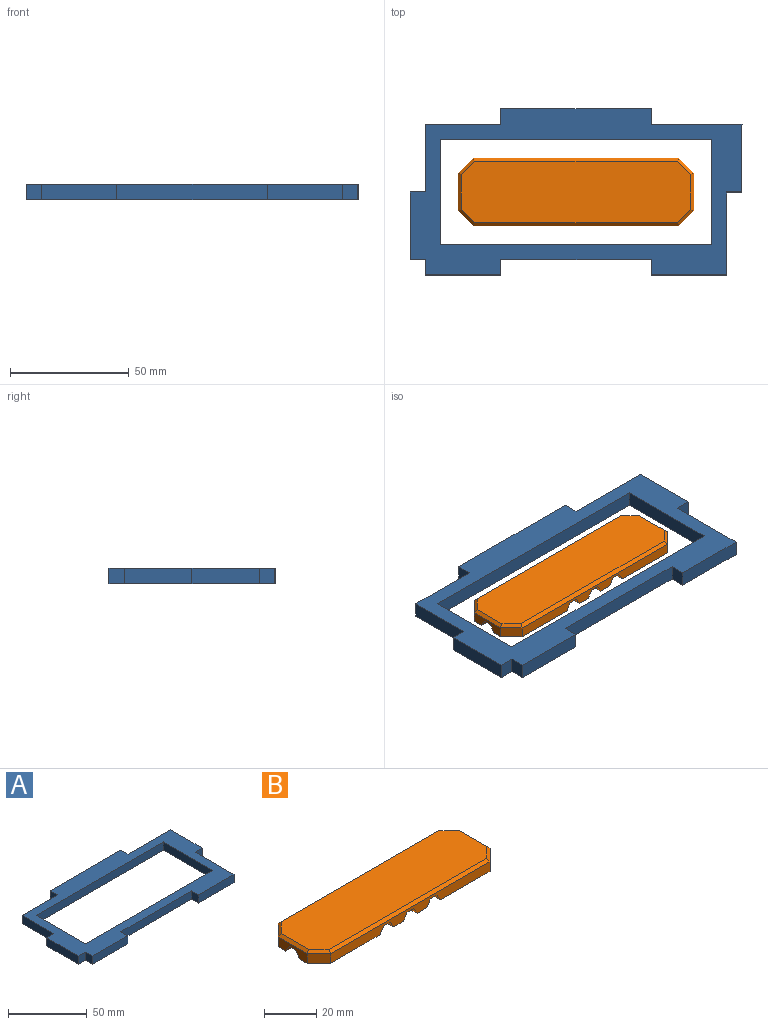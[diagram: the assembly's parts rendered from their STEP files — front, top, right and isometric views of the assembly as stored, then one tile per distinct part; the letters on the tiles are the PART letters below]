
ASSEMBLY  parts=2 mates=1
PART A: 24 faces, bbox 139.7x69.9x6.4 mm
  f0: plane 44.45x6.35mm, normal (-1,0,0), area 282.3mm2, adj f1,f21,f22,f23
  f1: plane 114.3x6.35mm, normal (0,1,0), area 725.8mm2, adj f0,f2,f22,f23
  f2: plane 44.45x6.35mm, normal (1,0,0), area 282.3mm2, adj f1,f21,f22,f23
  f3: plane 6.35x6.35mm, normal (1,0,0), area 40.3mm2, adj f4,f20,f22,f23
  f4: plane 63.5x6.35mm, normal (0,-1,0), area 403.2mm2, adj f3,f5,f22,f23
  f5: plane 6.35x6.35mm, normal (-1,0,0), area 40.3mm2, adj f4,f6,f22,f23
  f6: plane 31.75x6.35mm, normal (0,-1,0), area 201.6mm2, adj f5,f7,f22,f23
  f7: plane 34.93x6.35mm, normal (1,0,0), area 221.8mm2, adj f6,f8,f22,f23
  f8: plane 6.35x6.35mm, normal (0,-1,0), area 40.3mm2, adj f7,f9,f22,f23
  f9: plane 28.58x6.35mm, normal (1,0,0), area 181.5mm2, adj f8,f10,f22,f23
  f10: plane 38.1x6.35mm, normal (0,1,0), area 241.9mm2, adj f9,f11,f22,f23
  f11: plane 6.35x6.35mm, normal (1,0,0), area 40.3mm2, adj f10,f12,f22,f23
  f12: plane 63.5x6.35mm, normal (0,1,0), area 403.2mm2, adj f11,f13,f22,f23
  f13: plane 6.35x6.35mm, normal (-1,0,0), area 40.3mm2, adj f12,f14,f22,f23
  f14: plane 31.75x6.35mm, normal (0,1,0), area 201.6mm2, adj f13,f15,f22,f23
  f15: plane 28.58x6.35mm, normal (-1,0,0), area 181.5mm2, adj f14,f16,f22,f23
  f16: plane 6.35x6.35mm, normal (0,1,0), area 40.3mm2, adj f15,f17,f22,f23
  f17: plane 28.58x6.35mm, normal (-1,0,0), area 181.5mm2, adj f16,f18,f22,f23
  f18: plane 6.35x6.35mm, normal (0,-1,0), area 40.3mm2, adj f17,f19,f22,f23
  f19: plane 6.35x6.35mm, normal (-1,0,0), area 40.3mm2, adj f18,f20,f22,f23
  f20: plane 31.75x6.35mm, normal (0,-1,0), area 201.6mm2, adj f3,f19,f22,f23
  f21: plane 114.3x6.35mm, normal (0,-1,0), area 725.8mm2, adj f0,f2,f22,f23
  f22: plane 139.7x69.85mm, normal (0,0,1), area 3346.8mm2, adj f0,f1,f2,f3,f4,f5,f6,f7
  f23: plane 139.7x69.85mm, normal (0,0,-1), area 3346.8mm2, adj f0,f1,f2,f3,f4,f5,f6,f7
PART B: 42 faces, bbox 99.1x28.4x5.7 mm
  f0: plane 33.16x28.45mm, normal (0,0,-1), area 746.7mm2, adj f4,f5,f16,f17,f18,f20,f23,f24
  f1: plane 28.45x5.37mm, normal (0,0,-1), area 152.7mm2, adj f4,f5,f37,f40
  f2: plane 28.45x5.37mm, normal (0,0,-1), area 152.7mm2, adj f4,f5,f34,f36
  f3: plane 33.16x28.45mm, normal (0,0,-1), area 839.8mm2, adj f4,f5,f19,f21,f22,f27,f31,f33
  f4: plane 86.36x4.45mm, normal (0,1,0), area 331.5mm2, adj f0,f1,f2,f3,f10,f19,f20,f33
  f5: plane 86.36x4.45mm, normal (0,-1,0), area 331.5mm2, adj f0,f1,f2,f3,f8,f21,f23,f33
  f6: plane 96.52x25.91mm, normal (0,0,1), area 2437.8mm2, adj f7,f8,f9,f10,f11,f12,f13,f14
  f7: plane 15.75x1.27mm, normal (-0.71,0,0.71), area 27.3mm2, adj f6,f11,f12,f24
  f8: plane 86.36x1.27mm, normal (0,-0.71,0.71), area 154.2mm2, adj f5,f6,f12,f14
  f9: plane 15.75x1.27mm, normal (0.71,0,0.71), area 27.3mm2, adj f6,f13,f14,f22
  f10: plane 86.36x1.27mm, normal (0,0.71,0.71), area 154.2mm2, adj f4,f6,f11,f13
  f11: plane 6.88x6.88mm, normal (-0.5,0.5,0.71), area 15.2mm2, adj f6,f7,f10,f20
  f12: plane 6.88x6.88mm, normal (-0.5,-0.5,0.71), area 15.2mm2, adj f6,f7,f8,f23
  f13: plane 6.88x6.88mm, normal (0.5,0.5,0.71), area 15.2mm2, adj f6,f9,f10,f19
  f14: plane 6.88x6.88mm, normal (0.5,-0.5,0.71), area 15.2mm2, adj f6,f8,f9,f21
  f15: plane 12.7x3.67mm, normal (0,0,-1), area 46.6mm2, adj f16,f17,f18,f24
  f16: plane 7.33x3.18mm, normal (-1,0,0), area 17.5mm2, adj f0,f15,f17,f18
  f17: plane 12.7x3.18mm, normal (0,-0.87,-0.5), area 46.6mm2, adj f0,f15,f16,f24
  f18: plane 12.7x3.18mm, normal (0,0.87,-0.5), area 46.6mm2, adj f0,f15,f16,f24
  f19: plane 6.35x6.35mm, normal (0.71,0.71,0), area 39.9mm2, adj f3,f4,f13,f22
  f20: plane 6.35x6.35mm, normal (-0.71,0.71,0), area 39.9mm2, adj f0,f4,f11,f24
  f21: plane 6.35x6.35mm, normal (0.71,-0.71,0), area 39.9mm2, adj f3,f5,f14,f22
  f22: plane 15.75x4.45mm, normal (1,0,0), area 70mm2, adj f3,f9,f19,f21
  f23: plane 6.35x6.35mm, normal (-0.71,-0.71,0), area 39.9mm2, adj f0,f5,f12,f24
  f24: plane 15.75x4.45mm, normal (-1,0,0), area 52.5mm2, adj f0,f7,f15,f17,f18,f20,f23
  f25: cylinder r=3.17mm len=6.35mm, axis (0,0,-1), area 12.7mm2, adj f0,f26
  f26: plane 6.35x6.35mm, normal (0,0,-1), area 31.7mm2, adj f25
  f27: cylinder r=3.17mm len=6.35mm, axis (0,0,-1), area 12.7mm2, adj f3,f28
  f28: plane 6.35x6.35mm, normal (0,0,-1), area 31.7mm2, adj f27
  f29: cylinder r=3.17mm len=6.35mm, axis (0,0,-1), area 12.7mm2, adj f0,f30
  f30: plane 6.35x6.35mm, normal (0,0,-1), area 31.7mm2, adj f29
  f31: cylinder r=3.17mm len=6.35mm, axis (0,0,-1), area 12.7mm2, adj f3,f32
  f32: plane 6.35x6.35mm, normal (0,0,-1), area 31.7mm2, adj f31
  f33: plane 28.45x3.18mm, normal (-0.87,0,-0.5), area 104.3mm2, adj f3,f4,f5,f35
  f34: plane 28.45x3.18mm, normal (0.87,0,-0.5), area 104.3mm2, adj f2,f4,f5,f35
  f35: plane 28.45x3.67mm, normal (0,0,-1), area 104.3mm2, adj f4,f5,f33,f34
  f36: plane 28.45x3.18mm, normal (-0.87,0,-0.5), area 104.3mm2, adj f2,f4,f5,f38
  f37: plane 28.45x3.18mm, normal (0.87,0,-0.5), area 104.3mm2, adj f1,f4,f5,f38
  f38: plane 28.45x3.67mm, normal (0,0,-1), area 104.3mm2, adj f4,f5,f36,f37
  f39: plane 28.45x3.18mm, normal (0.87,0,-0.5), area 104.3mm2, adj f0,f4,f5,f41
  f40: plane 28.45x3.18mm, normal (-0.87,0,-0.5), area 104.3mm2, adj f1,f4,f5,f41
  f41: plane 28.45x3.67mm, normal (0,0,-1), area 104.3mm2, adj f4,f5,f39,f40
PLACE A t=(4.36,-5.88,0.96)mm
PLACE B t=(4.36,-5.88,-4.12)mm
MATE parallel B.f6 <-> A.f22  axis (0,0,1) through (4.36,-5.88,7.31)mm
